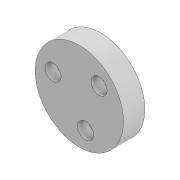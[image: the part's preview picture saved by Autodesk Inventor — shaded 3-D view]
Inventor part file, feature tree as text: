
AUTODESK INVENTOR PART (.ipt)
format: ipt  version: 2020.3 (Build 243373010, 373A)  size: 105,984 bytes
history: native  units: mm
features: extrude x2, sketch x2
ambient origin geometry x8: Origin, YZ Plane, XZ Plane, XY Plane, X Axis, Y Axis, Z Axis, Center Point
bodies: Solid1 (feature_tree)
feature tree (4):
  extrude  "Extrusion1"  Depth=20.0mm
  extrude  "Extrusion4"  Depth=10.0mm TaperAngle=0.0deg
  sketch  "Sketch1"  dims[d1=20.0mm d2=0.0mm d9=82.5mm]
  sketch  "Sketch4"  dims[d10=80.0mm d11=10.0mm d12=0.0mm d13=0.5mm d14=0.872665mm d15=0.5mm d16=0.872665mm]
